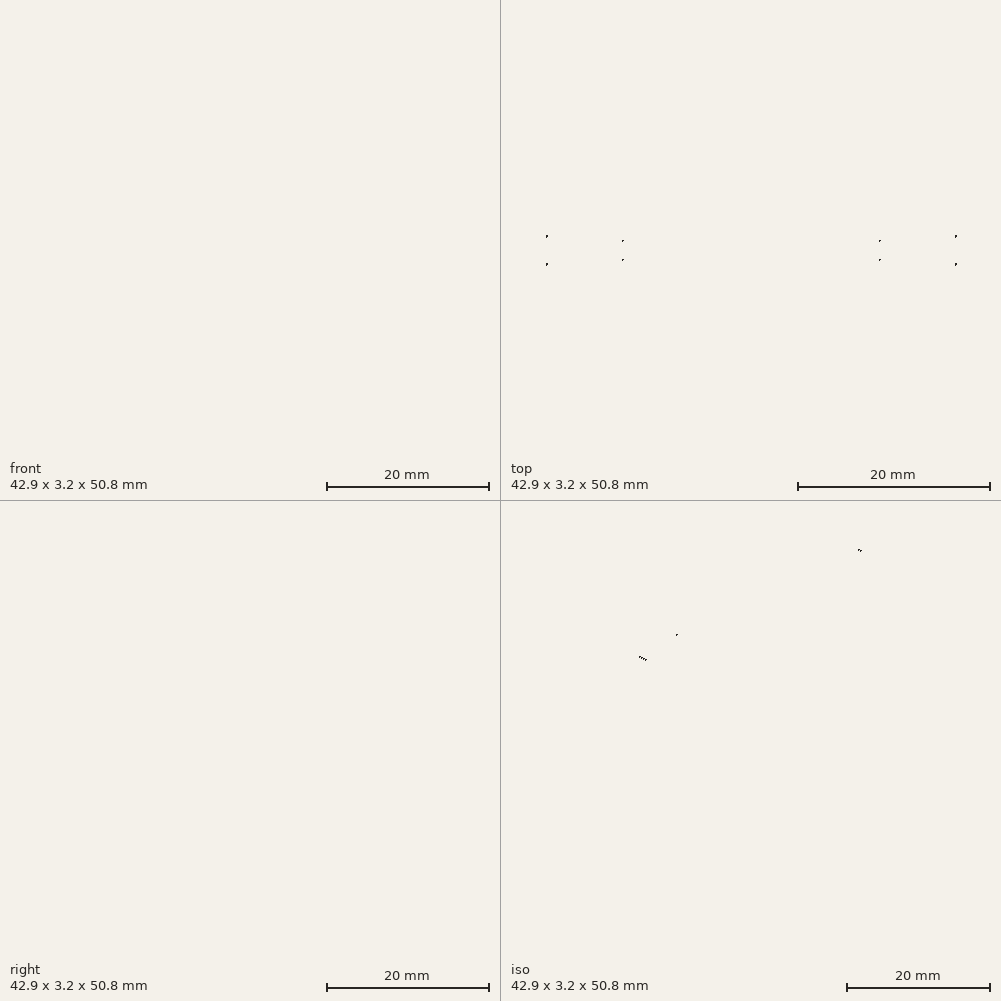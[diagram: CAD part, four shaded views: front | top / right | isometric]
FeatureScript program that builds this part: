
annotation { "Feature Type Name" : "Feature", "Feature Type Description" : "" }
export const myFeature = defineFeature(function(context is Context, id is Id, definition is map)
    precondition{}
    {
        {
            var Q0;
            Q0=qCreatedBy(makeId("Right.planeOp"),FACE);
            var sketch = newSketch(context, id + "F0", { "sketchPlane" : qUnion([Q0])});
            skLineSegment(sketch, "E0", {"start": v(0, 25.4) * mm, "end": v(0, -25.4) * mm, "construction": true});
            skLineSegment(sketch, "E1", {"start": v(-13.49, 25.4) * mm, "end": v(-21.44, 25.4) * mm});
            skLineSegment(sketch, "E2", {"start": v(-22.23, 24.61) * mm, "end": v(-22.23, 24.6) * mm});
            skLineSegment(sketch, "E3", {"start": v(-21.44, 23.81) * mm, "end": v(-15.88, 23.81) * mm});
            skLineSegment(sketch, "E4", {"start": v(-15.88, 23.81) * mm, "end": v(-15.87, -23.81) * mm});
            skLineSegment(sketch, "E5", {"start": v(-15.87, -23.81) * mm, "end": v(-21.44, -23.81) * mm});
            skLineSegment(sketch, "E6", {"start": v(-22.22, -24.6) * mm, "end": v(-22.22, -24.61) * mm});
            skLineSegment(sketch, "E7", {"start": v(-21.44, -25.4) * mm, "end": v(-13.49, -25.4) * mm});
            skLineSegment(sketch, "E8", {"start": v(-12.7, 24.61) * mm, "end": v(-12.7, -24.61) * mm});
            skPoint(sketch, "E9.visualSharp", {"position": v(-12.7, 25.4) * mm});
            skArc(sketch, "E9.filletArc", {"start": v(-12.7, 24.61) * mm, "mid": v(-12.93, 25.17) * mm, "end": v(-13.49, 25.4) * mm});
            skPoint(sketch, "E10.visualSharp", {"position": v(-22.23, 25.4) * mm});
            skArc(sketch, "E10.filletArc", {"start": v(-21.44, 25.4) * mm, "mid": v(-22, 25.17) * mm, "end": v(-22.23, 24.61) * mm});
            skPoint(sketch, "E11.visualSharp", {"position": v(-22.23, 23.81) * mm});
            skArc(sketch, "E11.filletArc", {"start": v(-22.23, 24.6) * mm, "mid": v(-22, 24.04) * mm, "end": v(-21.44, 23.81) * mm});
            skPoint(sketch, "E12.visualSharp", {"position": v(-12.7, -25.4) * mm});
            skArc(sketch, "E12.filletArc", {"start": v(-13.49, -25.4) * mm, "mid": v(-12.93, -25.17) * mm, "end": v(-12.7, -24.61) * mm});
            skPoint(sketch, "E13.visualSharp", {"position": v(-22.22, -25.4) * mm});
            skArc(sketch, "E13.filletArc", {"start": v(-22.22, -24.61) * mm, "mid": v(-22, -25.17) * mm, "end": v(-21.44, -25.4) * mm});
            skPoint(sketch, "E14.visualSharp", {"position": v(-22.22, -23.81) * mm});
            skArc(sketch, "E14.filletArc", {"start": v(-21.44, -23.81) * mm, "mid": v(-22, -24.04) * mm, "end": v(-22.22, -24.6) * mm});
            skSolve(sketch);
        }
        {
            var Q0;
            Q0=makeQuery(id+"F0.imprint","IMPRINT",FACE,{"disambiguationData":[TD([[makeQuery(id+"F0.imprint","IMPRINT",EDGE,{"derivedFrom":sQuery(id+"F0.wireOp",EDGE,"E1")}),1.0]])]});
            var Q1;
            Q1=sQuery(id+"F0.wireOp",EDGE,"E0");
            revolve(context, id + "F1", {"entities" : qUnion([Q0]), "axis" : qUnion([Q1]), "revolveType" : RevolveType.FULL});
        }
        {
            var Q0;
            Q0=qCreatedBy(makeId("Top.planeOp"),FACE);
            var sketch = newSketch(context, id + "F2", { "sketchPlane" : qUnion([Q0])});
            skLineSegment(sketch, "E15.rect.bottom", {"start": v(-25.4, 1.59) * mm, "end": v(25.4, 1.59) * mm});
            skLineSegment(sketch, "E15.rect.top", {"start": v(-25.4, -1.59) * mm, "end": v(25.4, -1.59) * mm});
            skLineSegment(sketch, "E15.rect.left", {"start": v(-25.4, 1.59) * mm, "end": v(-25.4, -1.59) * mm});
            skLineSegment(sketch, "E15.rect.right", {"start": v(25.4, 1.59) * mm, "end": v(25.4, -1.59) * mm});
            skPoint(sketch, "E15.rect.middle", {"position": v(0, 0) * mm});
            skSolve(sketch);
        }
        {
            var Q0;
            Q0=qSketchRegion(id+"F2",true);
            extrude(context, id + "F3", {"entities" : qUnion([Q0]), "operationType" : NewBodyOperationType.REMOVE, "endBound" : BoundingType.SYMMETRIC, "oppositeDirection" : true, "depth" : 50.8 * mm});
        }
        {
            var Q0;
            Q0=qCreatedBy(makeId("Front.planeOp"),FACE);
            var sketch = newSketch(context, id + "F4", { "sketchPlane" : qUnion([Q0])});
            skLineSegment(sketch, "E16.rect.bottom", {"start": v(25.4, 1.59) * mm, "end": v(-25.4, 1.59) * mm});
            skLineSegment(sketch, "E16.rect.top", {"start": v(25.4, -1.59) * mm, "end": v(-25.4, -1.59) * mm});
            skLineSegment(sketch, "E16.rect.left", {"start": v(25.4, 1.59) * mm, "end": v(25.4, -1.59) * mm});
            skLineSegment(sketch, "E16.rect.right", {"start": v(-25.4, 1.59) * mm, "end": v(-25.4, -1.59) * mm});
            skPoint(sketch, "E16.rect.middle", {"position": v(0, 0) * mm});
            skSolve(sketch);
        }
        {
            var Q0;
            Q0=makeQuery(id+"F4.imprint","IMPRINT",FACE,{"disambiguationData":[TD([[makeQuery(id+"F4.imprint","IMPRINT",EDGE,{"derivedFrom":sQuery(id+"F4.wireOp",EDGE,"E16.rect.bottom")}),1.0]])]});
            extrude(context, id + "F5", {"entities" : qUnion([Q0]), "operationType" : NewBodyOperationType.REMOVE, "endBound" : BoundingType.SYMMETRIC, "oppositeDirection" : true, "depth" : 50.8 * mm});
        }
        {
            var Q0;
            Q0=makeQuery(id+"F5.boolean.opBoolean","SPLIT",BODY,{"disambiguationData":[OD(0.0)],"derivedFrom":makeQuery(id+"F3.boolean.opBoolean","SPLIT",BODY,{"disambiguationData":[OD(0.0)],"derivedFrom":makeQuery(id+"F1.opRevolve","SWEPT_BODY",BODY,{"disambiguationData":[OSD([sQuery(id+"F0.wireOp",EDGE,"E1"),sQuery(id+"F0.wireOp",EDGE,"E2"),sQuery(id+"F0.wireOp",EDGE,"E3"),sQuery(id+"F0.wireOp",EDGE,"E4"),sQuery(id+"F0.wireOp",EDGE,"E5"),sQuery(id+"F0.wireOp",EDGE,"E6"),sQuery(id+"F0.wireOp",EDGE,"E7"),sQuery(id+"F0.wireOp",EDGE,"E8"),sQuery(id+"F0.wireOp",EDGE,"E9.filletArc"),sQuery(id+"F0.wireOp",EDGE,"E10.filletArc"),sQuery(id+"F0.wireOp",EDGE,"E11.filletArc"),sQuery(id+"F0.wireOp",EDGE,"E12.filletArc"),sQuery(id+"F0.wireOp",EDGE,"E13.filletArc"),sQuery(id+"F0.wireOp",EDGE,"E14.filletArc")])]})})});
            var Q1;
            Q1=makeQuery(id+"F5.boolean.opBoolean","SPLIT",BODY,{"disambiguationData":[OD(0.0)],"derivedFrom":makeQuery(id+"F3.boolean.opBoolean","SPLIT",BODY,{"disambiguationData":[OD(1.0)],"derivedFrom":makeQuery(id+"F1.opRevolve","SWEPT_BODY",BODY,{"disambiguationData":[OSD([sQuery(id+"F0.wireOp",EDGE,"E1"),sQuery(id+"F0.wireOp",EDGE,"E2"),sQuery(id+"F0.wireOp",EDGE,"E3"),sQuery(id+"F0.wireOp",EDGE,"E4"),sQuery(id+"F0.wireOp",EDGE,"E5"),sQuery(id+"F0.wireOp",EDGE,"E6"),sQuery(id+"F0.wireOp",EDGE,"E7"),sQuery(id+"F0.wireOp",EDGE,"E8"),sQuery(id+"F0.wireOp",EDGE,"E9.filletArc"),sQuery(id+"F0.wireOp",EDGE,"E10.filletArc"),sQuery(id+"F0.wireOp",EDGE,"E11.filletArc"),sQuery(id+"F0.wireOp",EDGE,"E12.filletArc"),sQuery(id+"F0.wireOp",EDGE,"E13.filletArc"),sQuery(id+"F0.wireOp",EDGE,"E14.filletArc")])]})})});
            deleteBodies(context, id + "F6", {"entities" : qUnion([Q0, Q1])});
        }
    });
